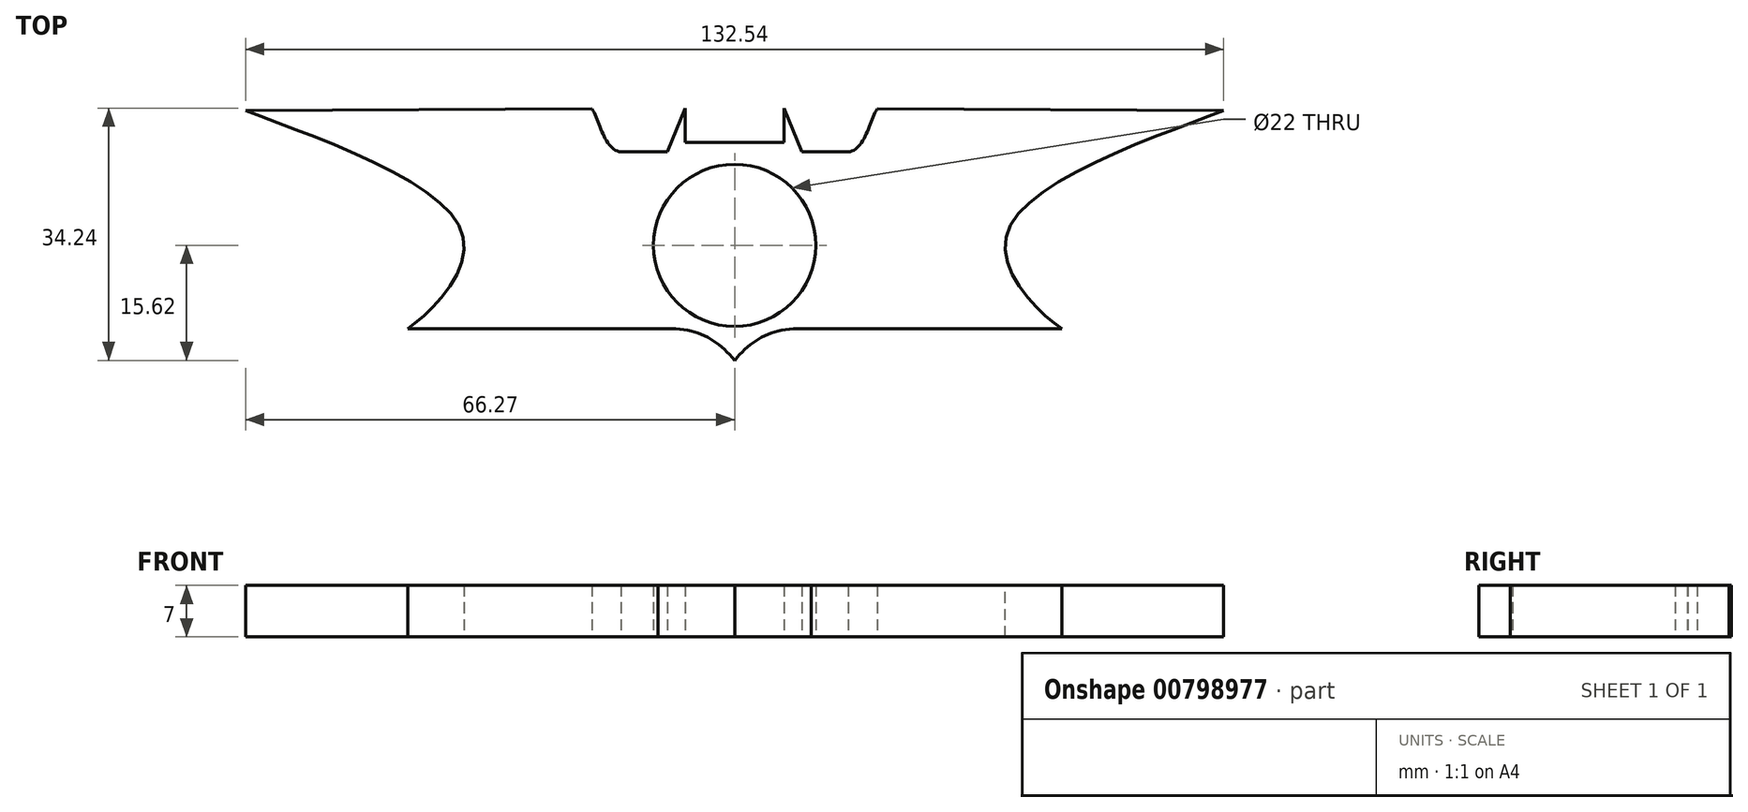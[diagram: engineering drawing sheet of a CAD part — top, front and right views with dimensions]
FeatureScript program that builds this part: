
annotation { "Feature Type Name" : "Feature", "Feature Type Description" : "" }
export const myFeature = defineFeature(function(context is Context, id is Id, definition is map)
    precondition{}
    {
        {
            var Q0;
            Q0=qCreatedBy(makeId("Top.planeOp"),FACE);
            var sketch = newSketch(context, id + "F0", { "sketchPlane" : qUnion([Q0])});
            skCircle(sketch, "E0", {"center": v(0, 0) * mm, "radius": 11 * mm});
            skLineSegment(sketch, "E1.bottom", {"start": v(0, -15.62) * mm, "end": v(0, -15.62) * mm});
            skLineSegment(sketch, "E1.top", {"start": v(0, 18.65) * mm, "end": v(0, 18.65) * mm});
            skLineSegment(sketch, "E2.bottom", {"start": v(-19.33, 18.55) * mm, "end": v(-67.99, 18.3) * mm});
            skLineSegment(sketch, "E3", {"start": v(0, 13.98) * mm, "end": v(-6.72, 13.98) * mm});
            skLineSegment(sketch, "E4", {"start": v(-6.72, 13.98) * mm, "end": v(-6.72, 18.62) * mm});
            skLineSegment(sketch, "E5", {"start": v(-6.72, 18.62) * mm, "end": v(-9.1, 12.7) * mm});
            skLineSegment(sketch, "E6", {"start": v(-9.1, 12.7) * mm, "end": v(-15.37, 12.66) * mm});
            skFitSpline(sketch, "E7", {"points": [v(-15.37, 12.66) * mm, v(-19.33, 18.55) * mm], "startDerivative": vector(-6.65, 0.52) * mm, "endDerivative": vector(-3.32, 5.75) * mm});
            skLineSegment(sketch, "E8", {"start": v(-19.33, 18.55) * mm, "end": v(-66.27, 18.31) * mm});
            skFitSpline(sketch, "E9", {"points": [v(-66.27, 18.31) * mm, v(-36.81, 1.27) * mm, v(-44.32, -11.32) * mm], "startDerivative": vector(43.4, -17.5) * mm, "endDerivative": vector(-20.78, -13.89) * mm});
            skLineSegment(sketch, "E10", {"start": v(-44.32, -11.32) * mm, "end": v(-10.37, -11.32) * mm});
            skFitSpline(sketch, "E11", {"points": [v(-10.37, -11.32) * mm, v(0, -15.62) * mm], "startDerivative": vector(14.75, 0.82) * mm, "endDerivative": vector(7.74, -9.64) * mm});
            skLineSegment(sketch, "E12.MirrorCS", {"start": v(0, 13.98) * mm, "end": v(6.72, 13.98) * mm});
            skLineSegment(sketch, "E13.MirrorCS", {"start": v(6.72, 13.98) * mm, "end": v(6.72, 18.62) * mm});
            skLineSegment(sketch, "E14.MirrorCS", {"start": v(6.72, 18.62) * mm, "end": v(9.1, 12.7) * mm});
            skLineSegment(sketch, "E15.MirrorCS", {"start": v(9.1, 12.7) * mm, "end": v(15.37, 12.66) * mm});
            skFitSpline(sketch, "E16.MirrorCS", {"points": [v(15.37, 12.66) * mm, v(19.33, 18.55) * mm], "startDerivative": vector(6.65, 0.52) * mm, "endDerivative": vector(3.32, 5.75) * mm});
            skLineSegment(sketch, "E17.MirrorCS", {"start": v(19.33, 18.55) * mm, "end": v(66.27, 18.31) * mm});
            skFitSpline(sketch, "E18.MirrorCS", {"points": [v(66.27, 18.31) * mm, v(36.81, 1.27) * mm, v(44.32, -11.32) * mm], "startDerivative": vector(-43.4, -17.5) * mm, "endDerivative": vector(20.78, -13.89) * mm});
            skLineSegment(sketch, "E19.MirrorCS", {"start": v(44.32, -11.32) * mm, "end": v(10.37, -11.32) * mm});
            skFitSpline(sketch, "E20.MirrorCS", {"points": [v(10.37, -11.32) * mm, v(0, -15.62) * mm], "startDerivative": vector(-14.75, 0.82) * mm, "endDerivative": vector(-7.74, -9.64) * mm});
            skLineSegment(sketch, "E21.trimOffspring", {"start": v(0, 11) * mm, "end": v(0, 13.98) * mm});
            skPoint(sketch, "E22.start.orphan", {"position": v(66.27, 26.62) * mm});
            skPoint(sketch, "E23.start.orphan", {"position": v(71.57, 18.31) * mm});
            skSolve(sketch);
        }
        {
            var Q0;
            Q0=makeQuery(id+"F0.imprint","IMPRINT",FACE,{"disambiguationData":[TD([[makeQuery(id+"F0.imprint","IMPRINT",EDGE,{"derivedFrom":sQuery(id+"F0.wireOp",EDGE,"E0")}),-1.0]])]});
            extrude(context, id + "F1", {"entities" : qUnion([Q0]), "depth" : 7 * mm, "offsetDistance" : 25.4 * mm});
        }
    });
